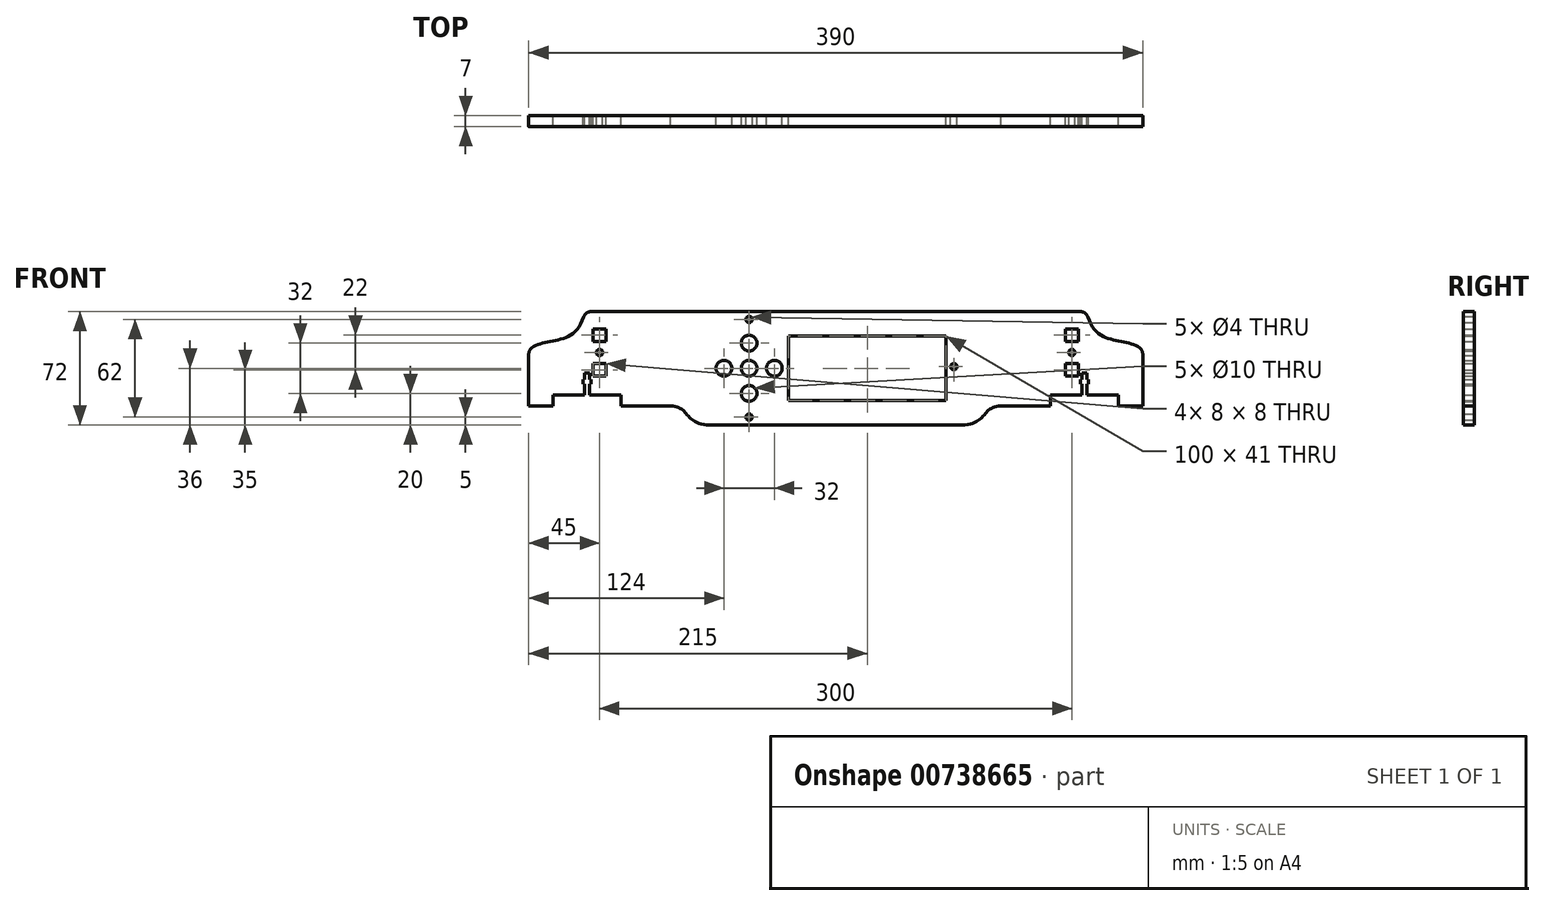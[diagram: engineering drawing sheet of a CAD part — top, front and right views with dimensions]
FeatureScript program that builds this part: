
annotation { "Feature Type Name" : "Feature", "Feature Type Description" : "" }
export const myFeature = defineFeature(function(context is Context, id is Id, definition is map)
    precondition{}
    {
        {
            var Q0;
            Q0=qCreatedBy(makeId("Front.planeOp"),FACE);
            var sketch = newSketch(context, id + "F0", { "sketchPlane" : qUnion([Q0])});
            skLineSegment(sketch, "E0", {"start": v(0, 0) * mm, "end": v(80, 0) * mm});
            skLineSegment(sketch, "E1", {"start": v(105, 12) * mm, "end": v(136.5, 12) * mm});
            skLineSegment(sketch, "E2", {"start": v(195, 12) * mm, "end": v(195, 44.93) * mm});
            skLineSegment(sketch, "E3", {"start": v(155.36, 72) * mm, "end": v(0, 72) * mm});
            skLineSegment(sketch, "E4", {"start": v(0, 0) * mm, "end": v(0, 72) * mm, "construction": true});
            skFitSpline(sketch, "E5", {"points": [v(159.19, 72) * mm, v(195, 47) * mm], "startDerivative": vector(16.3, -74.71) * mm, "endDerivative": vector(25.85, -31.58) * mm});
            skArc(sketch, "E6.filletArc", {"start": v(160.11, 68.54) * mm, "mid": v(158.3, 71.04) * mm, "end": v(155.36, 72) * mm});
            skArc(sketch, "E7.filletArc", {"start": v(195, 44.93) * mm, "mid": v(194.49, 47.13) * mm, "end": v(193.05, 48.89) * mm});
            skFitSpline(sketch, "E8", {"points": [v(80, 0) * mm, v(105, 12) * mm], "startDerivative": vector(48.85, 0) * mm, "endDerivative": vector(37.1, -0.37) * mm});
            skLineSegment(sketch, "E9", {"start": v(158, 12.14) * mm, "end": v(158, 33.14) * mm, "construction": true});
            skLineSegment(sketch, "E10", {"start": v(160.5, 29) * mm, "end": v(160.5, 26) * mm});
            skLineSegment(sketch, "E11", {"start": v(160.5, 26) * mm, "end": v(159.5, 26) * mm});
            skLineSegment(sketch, "E12", {"start": v(159.5, 19) * mm, "end": v(179.5, 19) * mm});
            skLineSegment(sketch, "E13", {"start": v(179.5, 19) * mm, "end": v(179.5, 12) * mm});
            skLineSegment(sketch, "E14", {"start": v(159.5, 19) * mm, "end": v(159.5, 26) * mm});
            skLineSegment(sketch, "E15", {"start": v(160.5, 29) * mm, "end": v(159.5, 29) * mm});
            skLineSegment(sketch, "E16", {"start": v(159.5, 29) * mm, "end": v(159.5, 33.14) * mm});
            skLineSegment(sketch, "E17", {"start": v(159.5, 33.14) * mm, "end": v(158, 33.14) * mm});
            skLineSegment(sketch, "E18.MirrorCS", {"start": v(156.5, 33.14) * mm, "end": v(158, 33.14) * mm});
            skLineSegment(sketch, "E19.MirrorCS", {"start": v(156.5, 29) * mm, "end": v(156.5, 33.14) * mm});
            skLineSegment(sketch, "E20.MirrorCS", {"start": v(155.5, 29) * mm, "end": v(156.5, 29) * mm});
            skLineSegment(sketch, "E21.MirrorCS", {"start": v(155.5, 29) * mm, "end": v(155.5, 26) * mm});
            skLineSegment(sketch, "E22.MirrorCS", {"start": v(155.5, 26) * mm, "end": v(156.5, 26) * mm});
            skLineSegment(sketch, "E23.MirrorCS", {"start": v(156.5, 19) * mm, "end": v(156.5, 26) * mm});
            skLineSegment(sketch, "E24.MirrorCS", {"start": v(156.5, 19) * mm, "end": v(136.5, 19) * mm});
            skLineSegment(sketch, "E25.MirrorCS", {"start": v(136.5, 19) * mm, "end": v(136.5, 12) * mm});
            skLineSegment(sketch, "E26.bottom", {"start": v(154, 31) * mm, "end": v(146, 31) * mm});
            skLineSegment(sketch, "E26.top", {"start": v(154, 39) * mm, "end": v(146, 39) * mm});
            skLineSegment(sketch, "E26.left", {"start": v(154, 31) * mm, "end": v(154, 39) * mm});
            skLineSegment(sketch, "E26.right", {"start": v(146, 31) * mm, "end": v(146, 39) * mm});
            skCircle(sketch, "E27", {"center": v(150, 46) * mm, "radius": 2 * mm});
            skPoint(sketch, "E27.centerSnap0", {"position": v(150, 39) * mm});
            skLineSegment(sketch, "E28", {"start": v(148, 46) * mm, "end": v(152, 46) * mm, "construction": true});
            skLineSegment(sketch, "E29.MirrorCS", {"start": v(146, 61) * mm, "end": v(146, 53) * mm});
            skLineSegment(sketch, "E30.MirrorCS", {"start": v(154, 53) * mm, "end": v(146, 53) * mm});
            skLineSegment(sketch, "E31.MirrorCS", {"start": v(154, 61) * mm, "end": v(154, 53) * mm});
            skLineSegment(sketch, "E32.MirrorCS", {"start": v(154, 61) * mm, "end": v(146, 61) * mm});
            skLineSegment(sketch, "E33.MirrorCS", {"start": v(-156.5, 33.14) * mm, "end": v(-158, 33.14) * mm});
            skLineSegment(sketch, "E34.MirrorCS", {"start": v(-155.5, 26) * mm, "end": v(-156.5, 26) * mm});
            skLineSegment(sketch, "E35.MirrorCS", {"start": v(-160.5, 29) * mm, "end": v(-160.5, 26) * mm});
            skLineSegment(sketch, "E36.MirrorCS", {"start": v(-160.5, 26) * mm, "end": v(-159.5, 26) * mm});
            skLineSegment(sketch, "E37.MirrorCS", {"start": v(-155.5, 29) * mm, "end": v(-156.5, 29) * mm});
            skLineSegment(sketch, "E38.MirrorCS", {"start": v(-159.5, 33.14) * mm, "end": v(-158, 33.14) * mm});
            skLineSegment(sketch, "E39.MirrorCS", {"start": v(-155.5, 29) * mm, "end": v(-155.5, 26) * mm});
            skLineSegment(sketch, "E40.MirrorCS", {"start": v(-156.5, 29) * mm, "end": v(-156.5, 33.14) * mm});
            skLineSegment(sketch, "E41.MirrorCS", {"start": v(-160.5, 29) * mm, "end": v(-159.5, 29) * mm});
            skLineSegment(sketch, "E42.MirrorCS", {"start": v(-159.5, 29) * mm, "end": v(-159.5, 33.14) * mm});
            skArc(sketch, "E43.MirrorCS", {"start": v(-195, 44.93) * mm, "mid": v(-194.49, 47.13) * mm, "end": v(-193.05, 48.89) * mm});
            skArc(sketch, "E44.MirrorCS", {"start": v(-160.11, 68.54) * mm, "mid": v(-158.3, 71.04) * mm, "end": v(-155.36, 72) * mm});
            skLineSegment(sketch, "E45.MirrorCS", {"start": v(-154, 31) * mm, "end": v(-154, 39) * mm});
            skLineSegment(sketch, "E46.MirrorCS", {"start": v(-148, 46) * mm, "end": v(-152, 46) * mm, "construction": true});
            skLineSegment(sketch, "E47.MirrorCS", {"start": v(-158, 12.14) * mm, "end": v(-158, 33.14) * mm, "construction": true});
            skLineSegment(sketch, "E48.MirrorCS", {"start": v(-179.5, 19) * mm, "end": v(-179.5, 12) * mm});
            skLineSegment(sketch, "E49.MirrorCS", {"start": v(-159.5, 19) * mm, "end": v(-159.5, 26) * mm});
            skLineSegment(sketch, "E50.MirrorCS", {"start": v(-154, 39) * mm, "end": v(-146, 39) * mm});
            skLineSegment(sketch, "E51.MirrorCS", {"start": v(-156.5, 19) * mm, "end": v(-156.5, 26) * mm});
            skLineSegment(sketch, "E52.MirrorCS", {"start": v(-146, 31) * mm, "end": v(-146, 39) * mm});
            skCircle(sketch, "E53.MirrorC", {"center": v(-150, 46) * mm, "radius": 2 * mm});
            skLineSegment(sketch, "E54.MirrorCS", {"start": v(-154, 61) * mm, "end": v(-154, 53) * mm});
            skPoint(sketch, "E55.MirrorP", {"position": v(-150, 39) * mm});
            skPoint(sketch, "E56.MirrorP", {"position": v(-159.19, 72) * mm});
            skLineSegment(sketch, "E57.MirrorCS", {"start": v(-154, 61) * mm, "end": v(-146, 61) * mm});
            skLineSegment(sketch, "E58.MirrorCS", {"start": v(-154, 31) * mm, "end": v(-146, 31) * mm});
            skLineSegment(sketch, "E59.MirrorCS", {"start": v(-136.5, 19) * mm, "end": v(-136.5, 12) * mm});
            skFitSpline(sketch, "E60.MirrorCS", {"points": [v(-80, 0) * mm, v(-105, 12) * mm], "startDerivative": vector(-48.85, 0) * mm, "endDerivative": vector(-37.1, -0.37) * mm});
            skLineSegment(sketch, "E61.MirrorCS", {"start": v(-159.5, 19) * mm, "end": v(-179.5, 19) * mm});
            skFitSpline(sketch, "E62.MirrorCS", {"points": [v(-159.19, 72) * mm, v(-195, 47) * mm], "startDerivative": vector(-16.3, -74.71) * mm, "endDerivative": vector(-25.85, -31.58) * mm});
            skLineSegment(sketch, "E63.MirrorCS", {"start": v(-155.36, 72) * mm, "end": v(0, 72) * mm});
            skLineSegment(sketch, "E64.MirrorCS", {"start": v(-195, 12) * mm, "end": v(-195, 44.93) * mm});
            skLineSegment(sketch, "E65.MirrorCS", {"start": v(-154, 53) * mm, "end": v(-146, 53) * mm});
            skLineSegment(sketch, "E66.MirrorCS", {"start": v(-156.5, 19) * mm, "end": v(-136.5, 19) * mm});
            skLineSegment(sketch, "E67.MirrorCS", {"start": v(-105, 12) * mm, "end": v(-136.5, 12) * mm});
            skLineSegment(sketch, "E68.MirrorCS", {"start": v(0, 0) * mm, "end": v(-80, 0) * mm});
            skLineSegment(sketch, "E69.MirrorCS", {"start": v(-146, 61) * mm, "end": v(-146, 53) * mm});
            skLineSegment(sketch, "E70.trimOffspring", {"start": v(179.5, 12) * mm, "end": v(195, 12) * mm});
            skLineSegment(sketch, "E71.trimOffspring", {"start": v(-179.5, 12) * mm, "end": v(-195, 12) * mm});
            skLineSegment(sketch, "E72.bottom", {"start": v(-30, 15.5) * mm, "end": v(70, 15.5) * mm});
            skLineSegment(sketch, "E72.top", {"start": v(-30, 56.5) * mm, "end": v(70, 56.5) * mm});
            skLineSegment(sketch, "E72.left", {"start": v(-30, 15.5) * mm, "end": v(-30, 56.5) * mm});
            skLineSegment(sketch, "E72.right", {"start": v(70, 15.5) * mm, "end": v(70, 56.5) * mm});
            skCircle(sketch, "E73", {"center": v(-55, 36) * mm, "radius": 5 * mm});
            skLineSegment(sketch, "E74", {"start": v(-60, 36) * mm, "end": v(-50, 36) * mm, "construction": true});
            skLineSegment(sketch, "E75", {"start": v(-55, 36) * mm, "end": v(-39, 36) * mm, "construction": true});
            skCircle(sketch, "E76", {"center": v(-39, 36) * mm, "radius": 5 * mm});
            skCircle(sketch, "E77.1.0", {"center": v(-55, 52) * mm, "radius": 5 * mm});
            skCircle(sketch, "E77.2.0", {"center": v(-71, 36) * mm, "radius": 5 * mm});
            skCircle(sketch, "E77.3.0", {"center": v(-55, 20) * mm, "radius": 5 * mm});
            skLineSegment(sketch, "E78", {"start": v(-55, 72) * mm, "end": v(-55, 0) * mm, "construction": true});
            skCircle(sketch, "E79", {"center": v(-55, 67) * mm, "radius": 2 * mm});
            skCircle(sketch, "E80.MirrorC", {"center": v(-55, 5) * mm, "radius": 2 * mm});
            skCircle(sketch, "E81", {"center": v(75, 37) * mm, "radius": 2 * mm});
            skSolve(sketch);
        }
        {
            var Q0;
            Q0 = qSketchRegion(id + "F0", true);
            extrude(context, id + "F1", {"entities" : qUnion([Q0]), "depth" : 7 * mm, "offsetDistance" : 25 * mm});
        }
    });
